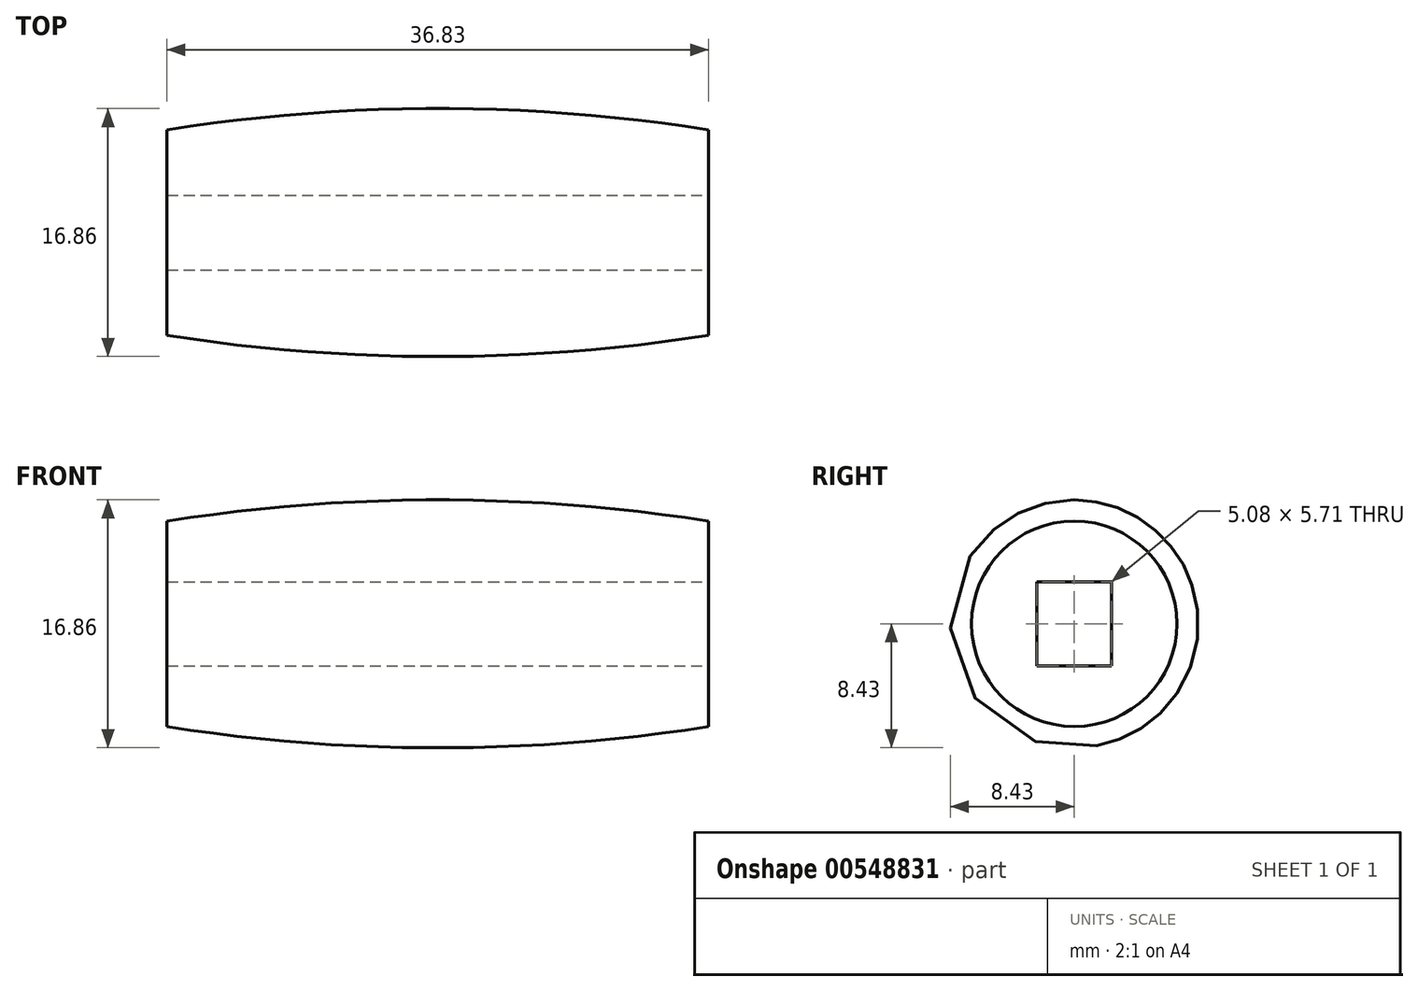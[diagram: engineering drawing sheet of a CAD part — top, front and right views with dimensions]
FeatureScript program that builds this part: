
annotation { "Feature Type Name" : "Feature", "Feature Type Description" : "" }
export const myFeature = defineFeature(function(context is Context, id is Id, definition is map)
    precondition{}
    {
        {
            var Q0;
            Q0=qCreatedBy(makeId("Front.planeOp"),FACE);
            var sketch = newSketch(context, id + "F0", { "sketchPlane" : qUnion([Q0])});
            skLineSegment(sketch, "E0", {"start": v(0, 0) * mm, "end": v(36.83, 0) * mm});
            skLineSegment(sketch, "E1", {"start": v(0, 0) * mm, "end": v(0, 6.99) * mm});
            skPoint(sketch, "E2", {"position": v(18.41, 0) * mm});
            skLineSegment(sketch, "E3.MirrorCS", {"start": v(36.83, 0) * mm, "end": v(36.83, 6.99) * mm});
            skArc(sketch, "E4", {"start": v(36.83, 6.99) * mm, "mid": v(18.42, 8.43) * mm, "end": v(0, 6.98) * mm});
            skSolve(sketch);
        }
        {
            var Q0;
            Q0=makeQuery(id+"F0.imprint","IMPRINT",FACE,{"disambiguationData":[TD([[makeQuery(id+"F0.imprint","IMPRINT",EDGE,{"derivedFrom":sQuery(id+"F0.wireOp",EDGE,"E0")}),1.0]])]});
            var Q1;
            Q1=sQuery(id+"F0.wireOp",EDGE,"E0");
            revolve(context, id + "F1", {"entities" : qUnion([Q0]), "axis" : qUnion([Q1]), "revolveType" : RevolveType.FULL});
        }
        {
            var Q0;
            Q0=makeQuery(id+"F1.opRevolve","SWEPT_FACE",FACE,{"disambiguationData":[OSD([sQuery(id+"F0.wireOp",EDGE,"E3.MirrorCS")])]});
            var sketch = newSketch(context, id + "F2", { "sketchPlane" : qUnion([Q0])});
            skLineSegment(sketch, "E5", {"start": v(2.54, 0) * mm, "end": v(2.54, 2.86) * mm});
            skLineSegment(sketch, "E6.MirrorCS", {"start": v(-2.54, 0) * mm, "end": v(-2.54, -2.86) * mm});
            skLineSegment(sketch, "E7.bottom", {"start": v(-2.54, -2.86) * mm, "end": v(2.54, -2.86) * mm});
            skLineSegment(sketch, "E7.top", {"start": v(-2.54, 2.86) * mm, "end": v(2.54, 2.86) * mm});
            skLineSegment(sketch, "E7.left", {"start": v(-2.54, -2.86) * mm, "end": v(-2.54, 2.86) * mm});
            skLineSegment(sketch, "E7.right", {"start": v(2.54, -2.86) * mm, "end": v(2.54, 2.86) * mm});
            skSolve(sketch);
        }
        {
            var Q0;
            {var subQ3=sQuery(id+"F2.wireOp",EDGE,"E7.bottom");Q0=makeQuery(id+"F2.imprint","IMPRINT",FACE,{"disambiguationData":[TD([[makeQuery(id+"F2.imprint","IMPRINT",EDGE,{"derivedFrom":subQ3}),1.0]])]});}
            extrude(context, id + "F3", {"entities" : qUnion([Q0]), "operationType" : NewBodyOperationType.REMOVE, "oppositeDirection" : true, "depth" : 45.97 * mm, "offsetDistance" : 25.4 * mm});
        }
    });
